# Revit family: Arper_Aava-02_chair_4woodlegs_wood_front-face-upholstery_7634
name_source: partatom
category: Furniture
units: mm (PartAtom-declared; Revit-internal decimal feet)

## family parameters
Always vertical = Yes
Cut with Voids When Loaded = No
OmniClass Number = 23.40.20.00
OmniClass Title = General Furniture and Specialties
Room Calculation Point = No
Shared = No
Work Plane-Based = No

## types (1)
- Arper_Aava-02_chair_4woodlegs_wood_front-face-upholstery_7634
    Arper - Legs material = Arper - L0006
    Default Elevation = 0 mm  [stored 0 ft]
    Description = Chair on a 4-leg base and shell in plywood with a reconstituted oak 
or walnut finish. Base and shell can be configured in the same finish, 
or by combining various wood finishes. The shell is upholstered in 
the front with fabric, leather, coated fabric or customer’s own 
material. Glides are also provided, with felt insert for wood floors.
    Manufacturer = ARPER s.p.a.
    Model = Aava 02
    URL = http://www.arper.com

note: [stored X ft] marks values corroborated as IEEE doubles in the binary element streams (Revit-internal decimal feet)
